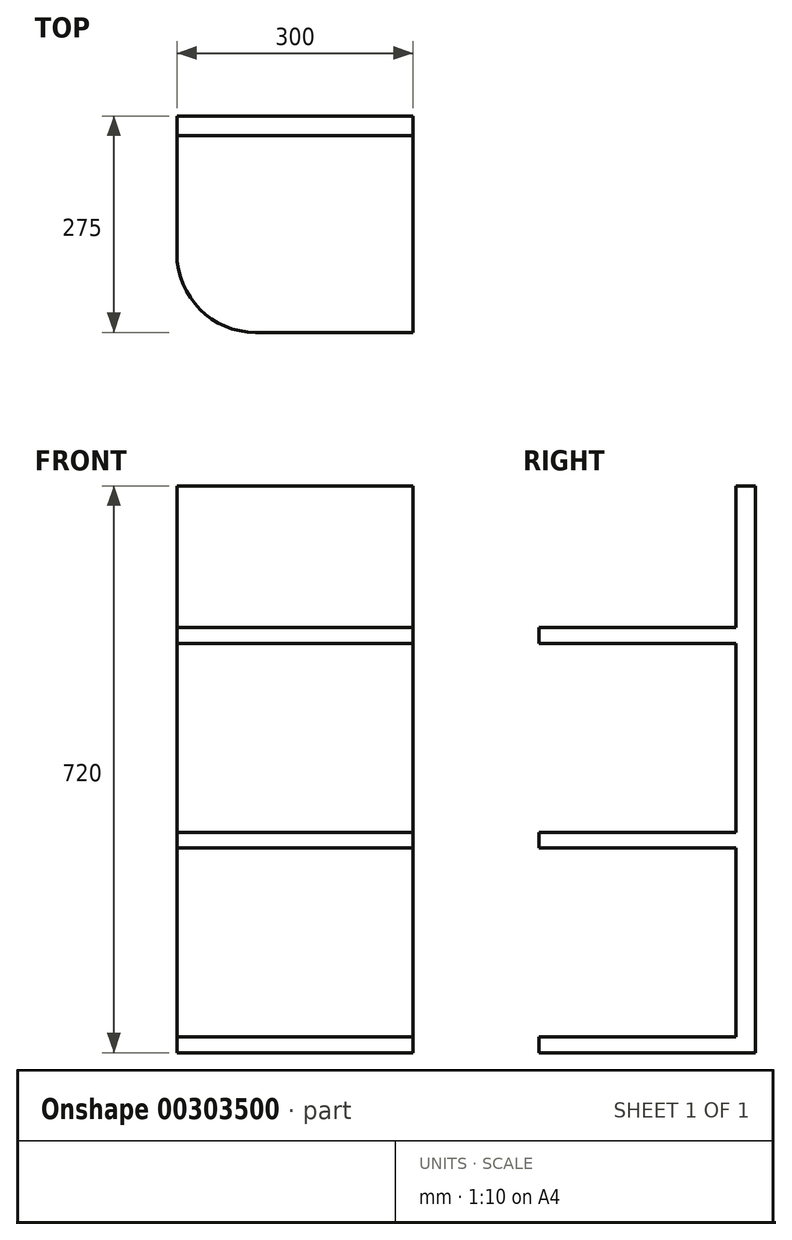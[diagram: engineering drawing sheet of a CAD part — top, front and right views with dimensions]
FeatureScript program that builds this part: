
annotation { "Feature Type Name" : "Feature", "Feature Type Description" : "" }
export const myFeature = defineFeature(function(context is Context, id is Id, definition is map)
    precondition{}
    {
        {
            var Q0;
            Q0=qCreatedBy(makeId("Front.planeOp"),FACE);
            var sketch = newSketch(context, id + "F0", { "sketchPlane" : qUnion([Q0])});
            skLineSegment(sketch, "E0.bottom", {"start": v(-300, 360) * mm, "end": v(0, 360) * mm});
            skLineSegment(sketch, "E0.top", {"start": v(-300, -360) * mm, "end": v(0, -360) * mm});
            skLineSegment(sketch, "E0.left", {"start": v(-300, 360) * mm, "end": v(-300, -360) * mm});
            skLineSegment(sketch, "E0.right", {"start": v(0, 360) * mm, "end": v(0, -360) * mm});
            skSolve(sketch);
        }
        {
            var Q0;
            Q0=makeQuery(id+"F0.imprint","IMPRINT",FACE,{"disambiguationData":[TD([[makeQuery(id+"F0.imprint","IMPRINT",EDGE,{"derivedFrom":sQuery(id+"F0.wireOp",EDGE,"E0.bottom")}),-1.0]])]});
            extrude(context, id + "F1", {"entities" : qUnion([Q0]), "depth" : 25 * mm});
        }
        {
            var Q0;
            Q0=makeQuery(id+"F1.opExtrude","CAP_FACE",FACE,{"disambiguationData":[OSD([sQuery(id+"F0.wireOp",EDGE,"E0.bottom"),sQuery(id+"F0.wireOp",EDGE,"E0.top"),sQuery(id+"F0.wireOp",EDGE,"E0.left"),sQuery(id+"F0.wireOp",EDGE,"E0.right")])],"isStart":false});
            var sketch = newSketch(context, id + "F2", { "sketchPlane" : qUnion([Q0])});
            skLineSegment(sketch, "E1.bottom", {"start": v(-300, -360) * mm, "end": v(0, -360) * mm});
            skLineSegment(sketch, "E1.top", {"start": v(-300, -340) * mm, "end": v(0, -340) * mm});
            skLineSegment(sketch, "E1.left", {"start": v(-300, -360) * mm, "end": v(-300, -340) * mm});
            skLineSegment(sketch, "E1.right", {"start": v(0, -360) * mm, "end": v(0, -340) * mm});
            skSolve(sketch);
        }
        {
            var Q0;
            Q0=makeQuery(id+"F2.imprint","IMPRINT",FACE,{"disambiguationData":[TD([[makeQuery(id+"F2.imprint","IMPRINT",EDGE,{"derivedFrom":sQuery(id+"F2.wireOp",EDGE,"E1.bottom")}),1.0]])]});
            extrude(context, id + "F3", {"entities" : qUnion([Q0]), "operationType" : NewBodyOperationType.ADD, "depth" : 250 * mm});
        }
        {
            var Q0;
            Q0=makeQuery(id+"F3.opExtrude","CAP_EDGE",EDGE,{"disambiguationData":[OSD([sQuery(id+"F2.wireOp",EDGE,"E1.left")])],"isStart":false});
            fillet(context, id + "F4", {"entities" : qUnion([Q0]), "radius" : 100 * mm, "tangentPropagation" : true, "allowEdgeOverflow" : false});
        }
        {
            var Q0;
            Q0=makeQuery(id+"F1.opExtrude","CAP_FACE",FACE,{"disambiguationData":[OSD([sQuery(id+"F0.wireOp",EDGE,"E0.bottom"),sQuery(id+"F0.wireOp",EDGE,"E0.top"),sQuery(id+"F0.wireOp",EDGE,"E0.left"),sQuery(id+"F0.wireOp",EDGE,"E0.right")])],"isStart":false});
            var sketch = newSketch(context, id + "F5", { "sketchPlane" : qUnion([Q0])});
            skLineSegment(sketch, "E2.bottom", {"start": v(-300, -100) * mm, "end": v(0, -100) * mm});
            skLineSegment(sketch, "E2.top", {"start": v(-300, -80) * mm, "end": v(0, -80) * mm});
            skLineSegment(sketch, "E2.left", {"start": v(-300, -100) * mm, "end": v(-300, -80) * mm});
            skLineSegment(sketch, "E2.right", {"start": v(0, -100) * mm, "end": v(0, -80) * mm});
            skLineSegment(sketch, "E3.bottom", {"start": v(-300, 160) * mm, "end": v(0, 160) * mm});
            skLineSegment(sketch, "E3.top", {"start": v(-300, 180) * mm, "end": v(0, 180) * mm});
            skLineSegment(sketch, "E3.left", {"start": v(-300, 160) * mm, "end": v(-300, 180) * mm});
            skLineSegment(sketch, "E3.right", {"start": v(0, 160) * mm, "end": v(0, 180) * mm});
            skSolve(sketch);
        }
        {
            var Q0;
            Q0=makeQuery(id+"F5.imprint","IMPRINT",FACE,{"disambiguationData":[TD([[makeQuery(id+"F5.imprint","IMPRINT",EDGE,{"derivedFrom":sQuery(id+"F5.wireOp",EDGE,"E2.bottom")}),1.0]])]});
            var Q1;
            Q1=makeQuery(id+"F5.imprint","IMPRINT",FACE,{"disambiguationData":[TD([[makeQuery(id+"F5.imprint","IMPRINT",EDGE,{"derivedFrom":sQuery(id+"F5.wireOp",EDGE,"E3.bottom")}),1.0]])]});
            extrude(context, id + "F6", {"entities" : qUnion([Q0, Q1]), "operationType" : NewBodyOperationType.ADD, "depth" : 250 * mm});
        }
        {
            var Q0;
            Q0=makeQuery(id+"F6.opExtrude","CAP_EDGE",EDGE,{"disambiguationData":[OSD([sQuery(id+"F5.wireOp",EDGE,"E3.left")])],"isStart":false});
            var Q1;
            Q1=makeQuery(id+"F6.opExtrude","CAP_EDGE",EDGE,{"disambiguationData":[OSD([sQuery(id+"F5.wireOp",EDGE,"E2.left")])],"isStart":false});
            fillet(context, id + "F7", {"entities" : qUnion([Q0, Q1]), "radius" : 100 * mm, "tangentPropagation" : true, "allowEdgeOverflow" : false});
        }
    });
